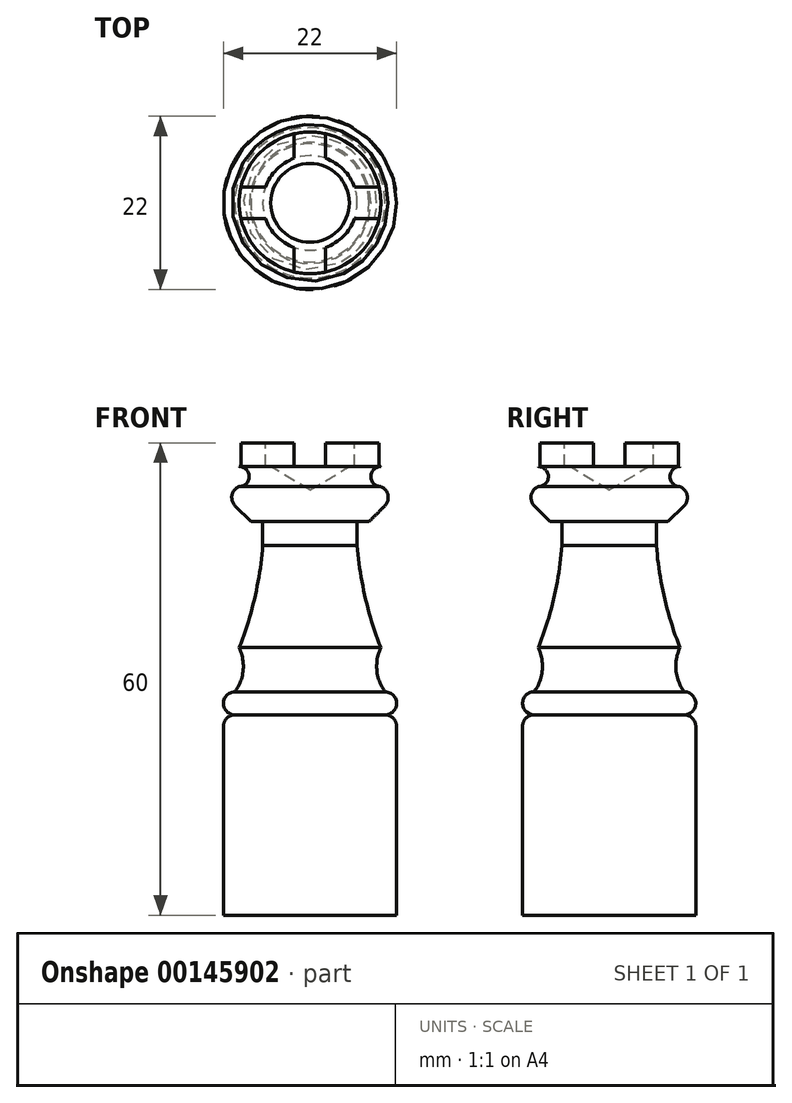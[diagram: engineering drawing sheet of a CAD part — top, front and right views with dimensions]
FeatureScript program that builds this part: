
annotation { "Feature Type Name" : "Feature", "Feature Type Description" : "" }
export const myFeature = defineFeature(function(context is Context, id is Id, definition is map)
    precondition{}
    {
        {
            var Q0;
            Q0=qCreatedBy(makeId("Top.planeOp"),FACE);
            var sketch = newSketch(context, id + "F0", { "sketchPlane" : qUnion([Q0])});
            skCircle(sketch, "E0", {"center": v(0, 0) * mm, "radius": 11 * mm});
            skSolve(sketch);
        }
        {
            var Q0;
            Q0=makeQuery(id+"F0.imprint","IMPRINT",FACE,{"disambiguationData":[TD([[makeQuery(id+"F0.imprint","IMPRINT",EDGE,{"derivedFrom":sQuery(id+"F0.wireOp",EDGE,"E0")}),1.0]])]});
            extrude(context, id + "F1", {"entities" : qUnion([Q0]), "depth" : 24 * mm});
        }
        {
            var Q0;
            Q0=qCreatedBy(makeId("Right.planeOp"),FACE);
            var sketch = newSketch(context, id + "F2", { "sketchPlane" : qUnion([Q0])});
            skLineSegment(sketch, "E1", {"start": v(0, 0) * mm, "end": v(0, 60) * mm, "construction": true});
            skLineSegment(sketch, "E2.0", {"start": v(-11, 24) * mm, "end": v(11, 24) * mm, "construction": true});
            skArc(sketch, "E3", {"start": v(11, 24) * mm, "mid": v(10.57, 25.03) * mm, "end": v(9.54, 25.46) * mm});
            skLineSegment(sketch, "E4", {"start": v(9.54, 24) * mm, "end": v(9.54, 28.38) * mm, "construction": true});
            skArc(sketch, "E5.MirrorC", {"start": v(9.54, 28.38) * mm, "mid": v(11, 26.92) * mm, "end": v(9.54, 25.46) * mm});
            skArc(sketch, "E6", {"start": v(9, 34) * mm, "mid": v(8.5, 31.12) * mm, "end": v(9.54, 28.38) * mm});
            skLineSegment(sketch, "E7", {"start": v(6, 50) * mm, "end": v(7.5, 50) * mm});
            skLineSegment(sketch, "E8", {"start": v(7.5, 50) * mm, "end": v(9.5, 52) * mm});
            skArc(sketch, "E9", {"start": v(9.5, 52) * mm, "mid": v(9.9, 53.36) * mm, "end": v(9, 54.45) * mm});
            skArc(sketch, "E10", {"start": v(9, 57) * mm, "mid": v(7.73, 55.73) * mm, "end": v(9, 54.45) * mm});
            skLineSegment(sketch, "E11", {"start": v(9, 57) * mm, "end": v(9, 60) * mm});
            skLineSegment(sketch, "E12", {"start": v(9, 60) * mm, "end": v(0, 60) * mm});
            skLineSegment(sketch, "E13", {"start": v(0, 60) * mm, "end": v(0, 24) * mm});
            skLineSegment(sketch, "E14", {"start": v(0, 24) * mm, "end": v(11, 24) * mm});
            skArc(sketch, "E15", {"start": v(6, 47) * mm, "mid": v(7, 40.39) * mm, "end": v(9, 34) * mm});
            skLineSegment(sketch, "E16", {"start": v(6, 50) * mm, "end": v(6, 47) * mm});
            skSolve(sketch);
        }
        {
            var Q0;
            Q0 = qSketchRegion(id + "F2", true);
            var Q1;
            Q1=sQuery(id+"F2.wireOp",EDGE,"E13");
            revolve(context, id + "F3", {"operationType" : NewBodyOperationType.ADD, "entities" : qUnion([Q0]), "axis" : qUnion([Q1]), "revolveType" : RevolveType.FULL});
        }
        {
            var Q0;
            Q0=makeQuery(id+"F3.opRevolve","SWEPT_FACE",FACE,{"disambiguationData":[OSD([sQuery(id+"F2.wireOp",EDGE,"E12")])]});
            var sketch = newSketch(context, id + "F4", { "sketchPlane" : qUnion([Q0])});
            skArc(sketch, "E17.0", {"start": v(2, 8.77) * mm, "mid": v(1, 8.94) * mm, "end": v(0, 9) * mm, "construction": true});
            skArc(sketch, "E18.0", {"start": v(-5.66, -2) * mm, "mid": v(-4.24, -4.24) * mm, "end": v(-2, -5.66) * mm});
            skLineSegment(sketch, "E19", {"start": v(0, 0) * mm, "end": v(0, 9) * mm, "construction": true});
            skLineSegment(sketch, "E20.0", {"start": v(2, 5.66) * mm, "end": v(2, 8.77) * mm});
            skLineSegment(sketch, "E21.MirrorCS", {"start": v(-2, 5.66) * mm, "end": v(-2, 8.77) * mm});
            skPoint(sketch, "E22.orphan", {"position": v(-2, 0) * mm});
            skPoint(sketch, "E23.orphan", {"position": v(2, 0) * mm});
            skPoint(sketch, "E24.orphan", {"position": v(-2, 13.1) * mm});
            skPoint(sketch, "E25.orphan", {"position": v(2, 13.1) * mm});
            skLineSegment(sketch, "E26.1.0", {"start": v(-5.66, -2) * mm, "end": v(-8.77, -2) * mm});
            skLineSegment(sketch, "E26.1.1", {"start": v(-5.66, 2) * mm, "end": v(-8.77, 2) * mm});
            skLineSegment(sketch, "E26.2.0", {"start": v(2, -5.66) * mm, "end": v(2, -8.77) * mm});
            skLineSegment(sketch, "E26.2.1", {"start": v(-2, -5.66) * mm, "end": v(-2, -8.77) * mm});
            skLineSegment(sketch, "E26.3.0", {"start": v(5.66, 2) * mm, "end": v(8.77, 2) * mm});
            skLineSegment(sketch, "E26.3.1", {"start": v(5.66, -2) * mm, "end": v(8.77, -2) * mm});
            skArc(sketch, "E27.0", {"start": v(-8.77, 2) * mm, "mid": v(-9, 0) * mm, "end": v(-8.77, -2) * mm});
            skArc(sketch, "E28.trimOffspring", {"start": v(2, 8.77) * mm, "mid": v(0, 9) * mm, "end": v(-2, 8.77) * mm});
            skArc(sketch, "E29.trimOffspring", {"start": v(8.77, -2) * mm, "mid": v(9, 0) * mm, "end": v(8.77, 2) * mm});
            skArc(sketch, "E30.trimOffspring", {"start": v(-2, -8.77) * mm, "mid": v(0, -9) * mm, "end": v(2, -8.77) * mm});
            skArc(sketch, "E31.trimOffspring", {"start": v(5.66, 2) * mm, "mid": v(4.24, 4.24) * mm, "end": v(2, 5.66) * mm});
            skArc(sketch, "E32.trimOffspring", {"start": v(2, -5.66) * mm, "mid": v(4.24, -4.24) * mm, "end": v(5.66, -2) * mm});
            skArc(sketch, "E33.trimOffspring", {"start": v(-2, 5.66) * mm, "mid": v(-4.24, 4.24) * mm, "end": v(-5.66, 2) * mm});
            skSolve(sketch);
        }
        {
            var Q0;
            Q0=makeQuery(id+"F4.imprint","IMPRINT",FACE,{"disambiguationData":[TD([[makeQuery(id+"F4.imprint","IMPRINT",EDGE,{"derivedFrom":sQuery(id+"F4.wireOp",EDGE,"E18.0")}),1.0]])]});
            extrude(context, id + "F5", {"entities" : qUnion([Q0]), "operationType" : NewBodyOperationType.REMOVE, "oppositeDirection" : true, "depth" : 3 * mm});
        }
        {
            var Q0;
            Q0=qCreatedBy(makeId("Right.planeOp"),FACE);
            var sketch = newSketch(context, id + "F6", { "sketchPlane" : qUnion([Q0])});
            skLineSegment(sketch, "E34", {"start": v(0, 57) * mm, "end": v(5, 57) * mm});
            skLineSegment(sketch, "E35", {"start": v(0, 57) * mm, "end": v(0, 54) * mm});
            skLineSegment(sketch, "E36", {"start": v(0, 54) * mm, "end": v(5, 57) * mm});
            skPoint(sketch, "E37.orphan", {"position": v(9, 57) * mm});
            skPoint(sketch, "E38.orphan", {"position": v(-9, 57) * mm});
            skSolve(sketch);
        }
        {
            var Q0;
            Q0 = qSketchRegion(id + "F6", true);
            var Q1;
            Q1=sQuery(id+"F6.wireOp",EDGE,"E35");
            revolve(context, id + "F7", {"operationType" : NewBodyOperationType.REMOVE, "entities" : qUnion([Q0]), "axis" : qUnion([Q1]), "revolveType" : RevolveType.FULL, "oppositeDirection" : true});
        }
    });
